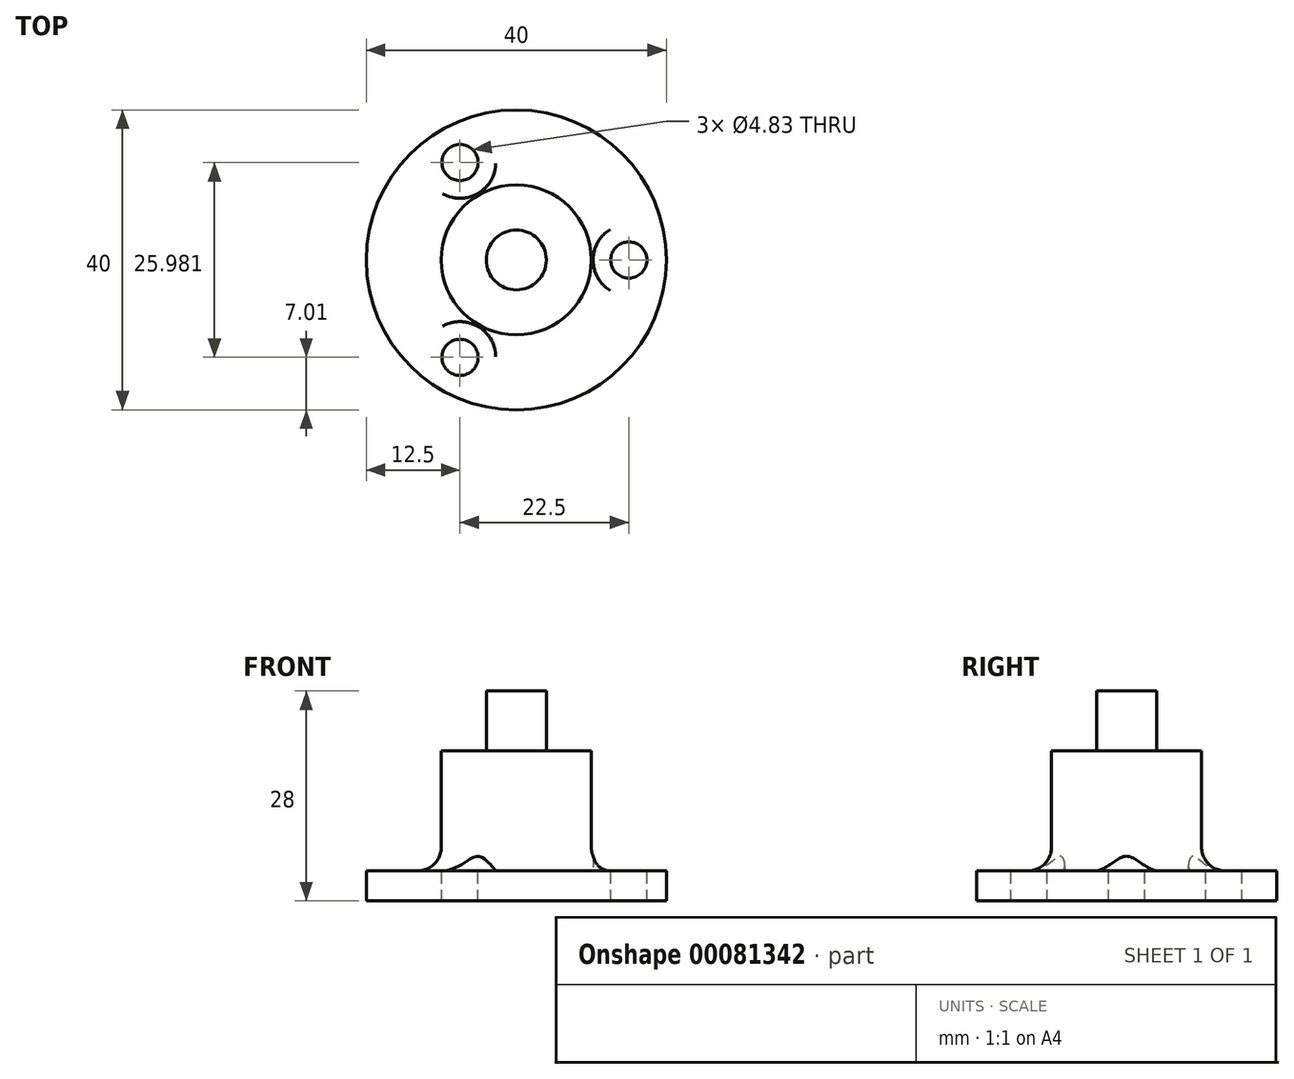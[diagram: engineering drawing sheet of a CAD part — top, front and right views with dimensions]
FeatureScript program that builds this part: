
annotation { "Feature Type Name" : "Feature", "Feature Type Description" : "" }
export const myFeature = defineFeature(function(context is Context, id is Id, definition is map)
    precondition{}
    {
        {
            var Q0;
            Q0=qCreatedBy(makeId("Front.planeOp"),FACE);
            var sketch = newSketch(context, id + "F0", { "sketchPlane" : qUnion([Q0])});
            skLineSegment(sketch, "E0", {"start": v(0, 0) * mm, "end": v(20, 0) * mm});
            skLineSegment(sketch, "E1", {"start": v(20, 0) * mm, "end": v(20, 4) * mm});
            skLineSegment(sketch, "E2", {"start": v(20, 4) * mm, "end": v(13.17, 4) * mm});
            skLineSegment(sketch, "E3", {"start": v(10, 20) * mm, "end": v(4, 20) * mm});
            skLineSegment(sketch, "E4", {"start": v(4, 20) * mm, "end": v(4, 28) * mm});
            skLineSegment(sketch, "E5", {"start": v(4, 28) * mm, "end": v(0, 28) * mm});
            skLineSegment(sketch, "E6", {"start": v(0, 28) * mm, "end": v(0, 0) * mm});
            skLineSegment(sketch, "E7", {"start": v(10, 20) * mm, "end": v(10, 7.18) * mm});
            skPoint(sketch, "E8.visualSharp", {"position": v(10, 4) * mm});
            skArc(sketch, "E8.filletArc", {"start": v(10, 7.18) * mm, "mid": v(10.93, 4.93) * mm, "end": v(13.17, 4) * mm});
            skSolve(sketch);
        }
        {
            var Q0;
            Q0=makeQuery(id+"F0.imprint","IMPRINT",FACE,{"disambiguationData":[TD([[makeQuery(id+"F0.imprint","IMPRINT",EDGE,{"derivedFrom":sQuery(id+"F0.wireOp",EDGE,"E0")}),1.0]])]});
            var Q1;
            Q1=sQuery(id+"F0.wireOp",EDGE,"E6");
            revolve(context, id + "F1", {"surfaceOperationType" : NewSurfaceOperationType.NEW, "entities" : qUnion([Q0]), "axis" : qUnion([Q1]), "revolveType" : RevolveType.FULL});
        }
        {
            var Q0;
            Q0=makeQuery(id+"F1.opRevolve","SWEPT_FACE",FACE,{"disambiguationData":[OSD([sQuery(id+"F0.wireOp",EDGE,"E2")])]});
            var sketch = newSketch(context, id + "F2", { "sketchPlane" : qUnion([Q0])});
            skCircle(sketch, "E9", {"center": v(15, 0) * mm, "radius": 2.41 * mm});
            skCircle(sketch, "E10", {"center": v(15, 0) * mm, "radius": 4.76 * mm});
            skCircle(sketch, "E11.1.0", {"center": v(-7.5, 13) * mm, "radius": 4.76 * mm});
            skCircle(sketch, "E11.1.1", {"center": v(-7.5, 13) * mm, "radius": 2.41 * mm});
            skCircle(sketch, "E11.2.0", {"center": v(-7.5, -13) * mm, "radius": 4.76 * mm});
            skCircle(sketch, "E11.2.1", {"center": v(-7.5, -13) * mm, "radius": 2.41 * mm});
            skPoint(sketch, "E11.center", {"position": v(0, 0) * mm});
            skSolve(sketch);
        }
        {
            var Q0;
            {var subQ0=sQuery(id+"F2.wireOp",EDGE,"E11.1.1");var subQ1=makeQuery(id+"F1.opRevolve","SWEPT_EDGE",EDGE,{"disambiguationData":[OSD([sQuery(id+"F0.wireOp",EDGE,"E2"),sQuery(id+"F0.wireOp",EDGE,"E8.filletArc")])]});var subQ2=makeQuery(id+"F2.imprint","INTERSECT",VERTEX,{"disambiguationData":[OD(0.0)],"derivedFrom":[subQ1,subQ0]});Q0=makeQuery(id+"F2.imprint","IMPRINT",FACE,{"disambiguationData":[TD([[makeQuery(id+"F2.imprint","IMPRINT",EDGE,{"disambiguationData":[TD([[subQ2,1.0]])],"derivedFrom":subQ0}),1.0]])]});}
            var Q1;
            {var subQ0=sQuery(id+"F2.wireOp",EDGE,"E11.1.1");var subQ1=makeQuery(id+"F1.opRevolve","SWEPT_EDGE",EDGE,{"disambiguationData":[OSD([sQuery(id+"F0.wireOp",EDGE,"E2"),sQuery(id+"F0.wireOp",EDGE,"E8.filletArc")])]});var subQ2=makeQuery(id+"F2.imprint","INTERSECT",VERTEX,{"disambiguationData":[OD(0.0)],"derivedFrom":[subQ1,subQ0]});Q1=makeQuery(id+"F2.imprint","IMPRINT",FACE,{"disambiguationData":[TD([[makeQuery(id+"F2.imprint","IMPRINT",EDGE,{"disambiguationData":[TD([[subQ2,-1.0]])],"derivedFrom":subQ0}),1.0]])]});}
            var Q2;
            {var subQ0=sQuery(id+"F2.wireOp",EDGE,"E9");var subQ1=makeQuery(id+"F1.opRevolve","SWEPT_EDGE",EDGE,{"disambiguationData":[OSD([sQuery(id+"F0.wireOp",EDGE,"E2"),sQuery(id+"F0.wireOp",EDGE,"E8.filletArc")])]});var subQ2=makeQuery(id+"F2.imprint","INTERSECT",VERTEX,{"disambiguationData":[OD(0.0)],"derivedFrom":[subQ1,subQ0]});Q2=makeQuery(id+"F2.imprint","IMPRINT",FACE,{"disambiguationData":[TD([[makeQuery(id+"F2.imprint","IMPRINT",EDGE,{"disambiguationData":[TD([[subQ2,1.0]])],"derivedFrom":subQ0}),1.0]])]});}
            var Q3;
            {var subQ0=sQuery(id+"F2.wireOp",EDGE,"E9");var subQ1=makeQuery(id+"F1.opRevolve","SWEPT_EDGE",EDGE,{"disambiguationData":[OSD([sQuery(id+"F0.wireOp",EDGE,"E2"),sQuery(id+"F0.wireOp",EDGE,"E8.filletArc")])]});var subQ2=makeQuery(id+"F2.imprint","INTERSECT",VERTEX,{"disambiguationData":[OD(0.0)],"derivedFrom":[subQ1,subQ0]});Q3=makeQuery(id+"F2.imprint","IMPRINT",FACE,{"disambiguationData":[TD([[makeQuery(id+"F2.imprint","IMPRINT",EDGE,{"disambiguationData":[TD([[subQ2,-1.0]])],"derivedFrom":subQ0}),1.0]])]});}
            var Q4;
            {var subQ0=sQuery(id+"F2.wireOp",EDGE,"E11.2.1");var subQ1=makeQuery(id+"F1.opRevolve","SWEPT_EDGE",EDGE,{"disambiguationData":[OSD([sQuery(id+"F0.wireOp",EDGE,"E2"),sQuery(id+"F0.wireOp",EDGE,"E8.filletArc")])]});var subQ2=makeQuery(id+"F2.imprint","INTERSECT",VERTEX,{"disambiguationData":[OD(0.0)],"derivedFrom":[subQ1,subQ0]});Q4=makeQuery(id+"F2.imprint","IMPRINT",FACE,{"disambiguationData":[TD([[makeQuery(id+"F2.imprint","IMPRINT",EDGE,{"disambiguationData":[TD([[subQ2,1.0]])],"derivedFrom":subQ0}),1.0]])]});}
            var Q5;
            {var subQ0=sQuery(id+"F2.wireOp",EDGE,"E11.2.1");var subQ1=makeQuery(id+"F1.opRevolve","SWEPT_EDGE",EDGE,{"disambiguationData":[OSD([sQuery(id+"F0.wireOp",EDGE,"E2"),sQuery(id+"F0.wireOp",EDGE,"E8.filletArc")])]});var subQ2=makeQuery(id+"F2.imprint","INTERSECT",VERTEX,{"disambiguationData":[OD(0.0)],"derivedFrom":[subQ1,subQ0]});Q5=makeQuery(id+"F2.imprint","IMPRINT",FACE,{"disambiguationData":[TD([[makeQuery(id+"F2.imprint","IMPRINT",EDGE,{"disambiguationData":[TD([[subQ2,-1.0]])],"derivedFrom":subQ0}),1.0]])]});}
            extrude(context, id + "F3", {"entities" : qUnion([Q0, Q1, Q2, Q3, Q4, Q5]), "operationType" : NewBodyOperationType.REMOVE, "oppositeDirection" : true, "depth" : 25.4 * mm, "offsetDistance" : 25.4 * mm, "symmetric" : true});
        }
        {
            var Q0;
            {var subQ0=sQuery(id+"F2.wireOp",EDGE,"E11.1.0");var subQ1=makeQuery(id+"F1.opRevolve","SWEPT_EDGE",EDGE,{"disambiguationData":[OSD([sQuery(id+"F0.wireOp",EDGE,"E2"),sQuery(id+"F0.wireOp",EDGE,"E8.filletArc")])]});var subQ2=makeQuery(id+"F2.imprint","INTERSECT",VERTEX,{"disambiguationData":[OD(0.0)],"derivedFrom":[subQ1,subQ0]});Q0=makeQuery(id+"F2.imprint","IMPRINT",FACE,{"disambiguationData":[TD([[makeQuery(id+"F2.imprint","IMPRINT",EDGE,{"disambiguationData":[TD([[subQ2,-1.0]])],"derivedFrom":subQ0}),1.0]])]});}
            var Q1;
            {var subQ0=sQuery(id+"F2.wireOp",EDGE,"E11.1.0");var subQ1=makeQuery(id+"F1.opRevolve","SWEPT_EDGE",EDGE,{"disambiguationData":[OSD([sQuery(id+"F0.wireOp",EDGE,"E2"),sQuery(id+"F0.wireOp",EDGE,"E8.filletArc")])]});var subQ2=makeQuery(id+"F2.imprint","INTERSECT",VERTEX,{"disambiguationData":[OD(0.0)],"derivedFrom":[subQ1,subQ0]});Q1=makeQuery(id+"F2.imprint","IMPRINT",FACE,{"disambiguationData":[TD([[makeQuery(id+"F2.imprint","IMPRINT",EDGE,{"disambiguationData":[TD([[subQ2,1.0]])],"derivedFrom":subQ0}),1.0]])]});}
            var Q2;
            {var subQ0=sQuery(id+"F2.wireOp",EDGE,"E9");var subQ1=makeQuery(id+"F1.opRevolve","SWEPT_EDGE",EDGE,{"disambiguationData":[OSD([sQuery(id+"F0.wireOp",EDGE,"E2"),sQuery(id+"F0.wireOp",EDGE,"E8.filletArc")])]});var subQ2=makeQuery(id+"F2.imprint","INTERSECT",VERTEX,{"disambiguationData":[OD(0.0)],"derivedFrom":[subQ1,subQ0]});Q2=makeQuery(id+"F2.imprint","IMPRINT",FACE,{"disambiguationData":[TD([[makeQuery(id+"F2.imprint","IMPRINT",EDGE,{"disambiguationData":[TD([[subQ2,-1.0]])],"derivedFrom":subQ0}),-1.0]])]});}
            var Q3;
            {var subQ0=sQuery(id+"F2.wireOp",EDGE,"E9");var subQ1=makeQuery(id+"F1.opRevolve","SWEPT_EDGE",EDGE,{"disambiguationData":[OSD([sQuery(id+"F0.wireOp",EDGE,"E2"),sQuery(id+"F0.wireOp",EDGE,"E8.filletArc")])]});var subQ2=makeQuery(id+"F2.imprint","INTERSECT",VERTEX,{"disambiguationData":[OD(0.0)],"derivedFrom":[subQ1,subQ0]});Q3=makeQuery(id+"F2.imprint","IMPRINT",FACE,{"disambiguationData":[TD([[makeQuery(id+"F2.imprint","IMPRINT",EDGE,{"disambiguationData":[TD([[subQ2,1.0]])],"derivedFrom":subQ0}),-1.0]])]});}
            var Q4;
            {var subQ0=sQuery(id+"F2.wireOp",EDGE,"E11.2.0");var subQ1=makeQuery(id+"F1.opRevolve","SWEPT_EDGE",EDGE,{"disambiguationData":[OSD([sQuery(id+"F0.wireOp",EDGE,"E2"),sQuery(id+"F0.wireOp",EDGE,"E8.filletArc")])]});var subQ2=makeQuery(id+"F2.imprint","INTERSECT",VERTEX,{"disambiguationData":[OD(0.0)],"derivedFrom":[subQ1,subQ0]});Q4=makeQuery(id+"F2.imprint","IMPRINT",FACE,{"disambiguationData":[TD([[makeQuery(id+"F2.imprint","IMPRINT",EDGE,{"disambiguationData":[TD([[subQ2,1.0]])],"derivedFrom":subQ0}),1.0]])]});}
            var Q5;
            {var subQ0=sQuery(id+"F2.wireOp",EDGE,"E11.2.0");var subQ1=makeQuery(id+"F1.opRevolve","SWEPT_EDGE",EDGE,{"disambiguationData":[OSD([sQuery(id+"F0.wireOp",EDGE,"E2"),sQuery(id+"F0.wireOp",EDGE,"E8.filletArc")])]});var subQ2=makeQuery(id+"F2.imprint","INTERSECT",VERTEX,{"disambiguationData":[OD(0.0)],"derivedFrom":[subQ1,subQ0]});Q5=makeQuery(id+"F2.imprint","IMPRINT",FACE,{"disambiguationData":[TD([[makeQuery(id+"F2.imprint","IMPRINT",EDGE,{"disambiguationData":[TD([[subQ2,-1.0]])],"derivedFrom":subQ0}),1.0]])]});}
            extrude(context, id + "F4", {"entities" : qUnion([Q0, Q1, Q2, Q3, Q4, Q5]), "operationType" : NewBodyOperationType.REMOVE, "endBound" : BoundingType.THROUGH_ALL, "depth" : 25.4 * mm, "offsetDistance" : 25.4 * mm});
        }
    });
